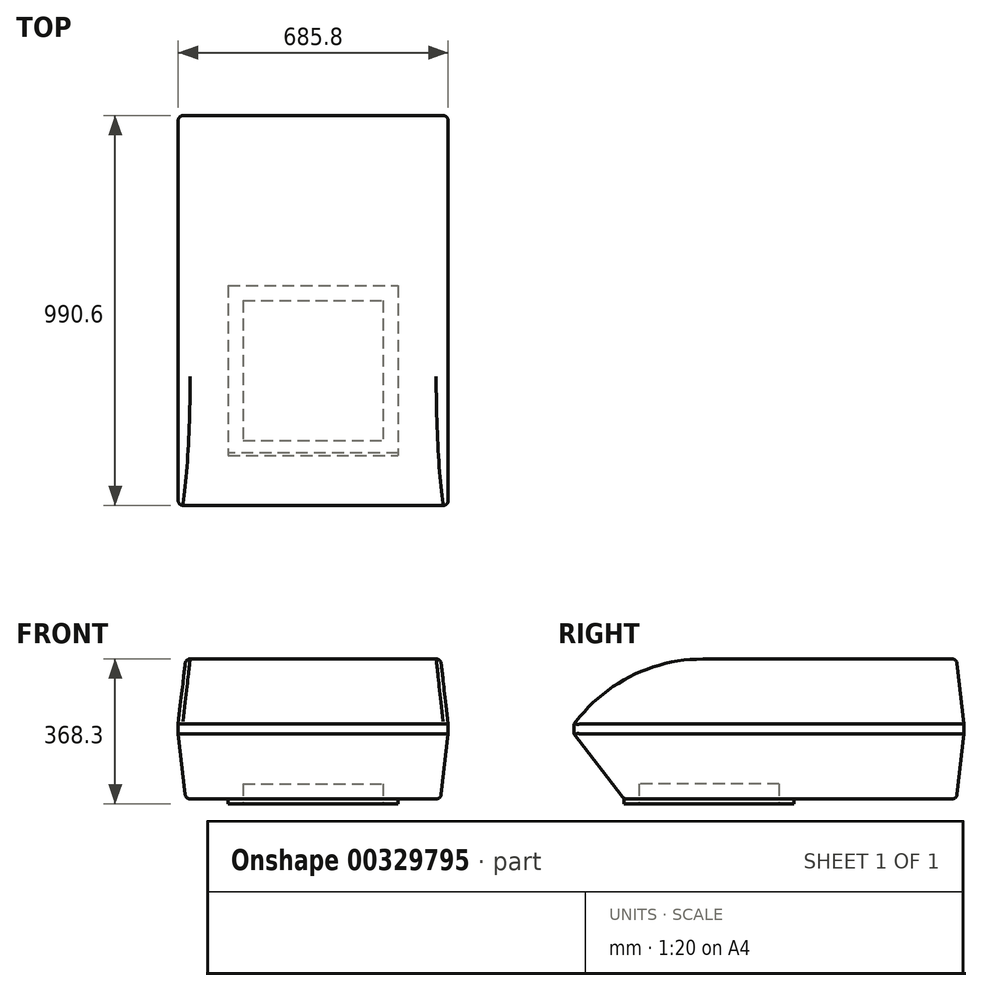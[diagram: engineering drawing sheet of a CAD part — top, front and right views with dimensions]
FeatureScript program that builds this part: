
annotation { "Feature Type Name" : "Feature", "Feature Type Description" : "" }
export const myFeature = defineFeature(function(context is Context, id is Id, definition is map)
    precondition{}
    {
        {
            var Q0;
            Q0=qCreatedBy(makeId("Top.planeOp"),FACE);
            var sketch = newSketch(context, id + "F0", { "sketchPlane" : qUnion([Q0])});
            skLineSegment(sketch, "E0.bottom", {"start": v(0, 0) * mm, "end": v(-685.8, 0) * mm});
            skLineSegment(sketch, "E0.top", {"start": v(0, 990.6) * mm, "end": v(-685.8, 990.6) * mm});
            skLineSegment(sketch, "E0.left", {"start": v(0, 0) * mm, "end": v(0, 990.6) * mm});
            skLineSegment(sketch, "E0.right", {"start": v(-685.8, 0) * mm, "end": v(-685.8, 990.6) * mm});
            skSolve(sketch);
        }
        {
            var Q0;
            Q0 = qSketchRegion(id + "F0", true);
            extrude(context, id + "F1", {"entities" : qUnion([Q0]), "depth" : 355.6 * mm});
        }
        {
            var Q0;
            Q0=makeQuery(id+"F1.opExtrude","CAP_FACE",FACE,{"disambiguationData":[OSD([sQuery(id+"F0.wireOp",EDGE,"E0.bottom"),sQuery(id+"F0.wireOp",EDGE,"E0.top"),sQuery(id+"F0.wireOp",EDGE,"E0.left"),sQuery(id+"F0.wireOp",EDGE,"E0.right")])],"isStart":true});
            var sketch = newSketch(context, id + "F2", { "sketchPlane" : qUnion([Q0])});
            skLineSegment(sketch, "E1.bottom", {"start": v(-520.7, -520.7) * mm, "end": v(-165.1, -520.7) * mm});
            skLineSegment(sketch, "E1.top", {"start": v(-520.7, -165.1) * mm, "end": v(-165.1, -165.1) * mm});
            skLineSegment(sketch, "E1.left", {"start": v(-520.7, -520.7) * mm, "end": v(-520.7, -165.1) * mm});
            skLineSegment(sketch, "E1.right", {"start": v(-165.1, -520.7) * mm, "end": v(-165.1, -165.1) * mm});
            skLineSegment(sketch, "E2.0", {"start": v(-558.8, -558.8) * mm, "end": v(-558.8, -127) * mm});
            skLineSegment(sketch, "E2.1", {"start": v(-558.8, -558.8) * mm, "end": v(-127, -558.8) * mm});
            skLineSegment(sketch, "E2.2", {"start": v(-127, -558.8) * mm, "end": v(-127, -127) * mm});
            skLineSegment(sketch, "E2.3", {"start": v(-558.8, -127) * mm, "end": v(-127, -127) * mm});
            skSolve(sketch);
        }
        {
            var Q0;
            Q0=makeQuery(id+"F1.opExtrude","CAP_EDGE",EDGE,{"disambiguationData":[OSD([sQuery(id+"F0.wireOp",EDGE,"E0.right")])],"isStart":false});
            var Q1;
            Q1=makeQuery(id+"F1.opExtrude","CAP_EDGE",EDGE,{"disambiguationData":[OSD([sQuery(id+"F0.wireOp",EDGE,"E0.left")])],"isStart":false});
            var Q2;
            Q2=makeQuery(id+"F1.opExtrude","CAP_EDGE",EDGE,{"disambiguationData":[OSD([sQuery(id+"F0.wireOp",EDGE,"E0.right")])],"isStart":true});
            var Q3;
            Q3=makeQuery(id+"F1.opExtrude","CAP_EDGE",EDGE,{"disambiguationData":[OSD([sQuery(id+"F0.wireOp",EDGE,"E0.left")])],"isStart":true});
            var Q4;
            Q4=makeQuery(id+"F1.opExtrude","CAP_EDGE",EDGE,{"disambiguationData":[OSD([sQuery(id+"F0.wireOp",EDGE,"E0.top")])],"isStart":false});
            var Q5;
            Q5=makeQuery(id+"F1.opExtrude","CAP_EDGE",EDGE,{"disambiguationData":[OSD([sQuery(id+"F0.wireOp",EDGE,"E0.top")])],"isStart":true});
            chamfer(context, id + "F3", {"entities" : qUnion([Q0, Q1, Q2, Q3, Q4, Q5]), "chamferType" : ChamferType.TWO_OFFSETS, "width1" : 165.1 * mm, "oppositeDirection" : false, "width2" : 19.05 * mm, "tangentPropagation" : true});
        }
        {
            var Q0;
            Q0=makeQuery(id+"F1.opExtrude","CAP_EDGE",EDGE,{"disambiguationData":[OSD([sQuery(id+"F0.wireOp",EDGE,"E0.bottom")])],"isStart":false});
            var Q1;
            Q1=makeQuery(id+"F1.opExtrude","CAP_EDGE",EDGE,{"disambiguationData":[OSD([sQuery(id+"F0.wireOp",EDGE,"E0.bottom")])],"isStart":true});
            chamfer(context, id + "F4", {"entities" : qUnion([Q0, Q1]), "chamferType" : ChamferType.TWO_OFFSETS, "width1" : 165.1 * mm, "oppositeDirection" : false, "width2" : 127 * mm, "tangentPropagation" : true});
        }
        {
            var Q0;
            Q0=makeQuery(id+"F1.opExtrude","CAP_FACE",FACE,{"disambiguationData":[OSD([sQuery(id+"F0.wireOp",EDGE,"E0.bottom"),sQuery(id+"F0.wireOp",EDGE,"E0.top"),sQuery(id+"F0.wireOp",EDGE,"E0.left"),sQuery(id+"F0.wireOp",EDGE,"E0.right")])],"isStart":true});
            var Q1;
            Q1=makeQuery(id+"F1.opExtrude","SWEPT_EDGE",EDGE,{"disambiguationData":[OSD([sQuery(id+"F0.wireOp",EDGE,"E0.top"),sQuery(id+"F0.wireOp",EDGE,"E0.right")])]});
            var Q2;
            Q2=makeQuery(id+"F1.opExtrude","SWEPT_EDGE",EDGE,{"disambiguationData":[OSD([sQuery(id+"F0.wireOp",EDGE,"E0.top"),sQuery(id+"F0.wireOp",EDGE,"E0.left")])]});
            var Q3;
            Q3=makeQuery(id+"F3.opChamfer","BLEND_EDGE",EDGE,{"blendedFrom":[makeQuery(id+"F1.opExtrude","CAP_EDGE",EDGE,{"disambiguationData":[OSD([sQuery(id+"F0.wireOp",EDGE,"E0.top")])],"isStart":true}),makeQuery(id+"F1.opExtrude","CAP_EDGE",EDGE,{"disambiguationData":[OSD([sQuery(id+"F0.wireOp",EDGE,"E0.right")])],"isStart":true})],"blendedInto":[]});
            var Q4;
            Q4=makeQuery(id+"F3.opChamfer","BLEND_EDGE",EDGE,{"blendedFrom":[makeQuery(id+"F1.opExtrude","CAP_EDGE",EDGE,{"disambiguationData":[OSD([sQuery(id+"F0.wireOp",EDGE,"E0.top")])],"isStart":true}),makeQuery(id+"F1.opExtrude","CAP_EDGE",EDGE,{"disambiguationData":[OSD([sQuery(id+"F0.wireOp",EDGE,"E0.left")])],"isStart":true})],"blendedInto":[]});
            var Q5;
            Q5=makeQuery(id+"F3.opChamfer","BLEND_EDGE",EDGE,{"blendedFrom":[makeQuery(id+"F1.opExtrude","CAP_EDGE",EDGE,{"disambiguationData":[OSD([sQuery(id+"F0.wireOp",EDGE,"E0.top")])],"isStart":false}),makeQuery(id+"F1.opExtrude","CAP_EDGE",EDGE,{"disambiguationData":[OSD([sQuery(id+"F0.wireOp",EDGE,"E0.left")])],"isStart":false})],"blendedInto":[]});
            var Q6;
            Q6=makeQuery(id+"F3.opChamfer","BLEND_EDGE",EDGE,{"blendedFrom":[makeQuery(id+"F1.opExtrude","CAP_EDGE",EDGE,{"disambiguationData":[OSD([sQuery(id+"F0.wireOp",EDGE,"E0.top")])],"isStart":false}),makeQuery(id+"F1.opExtrude","CAP_EDGE",EDGE,{"disambiguationData":[OSD([sQuery(id+"F0.wireOp",EDGE,"E0.right")])],"isStart":false})],"blendedInto":[]});
            var Q7;
            Q7=makeQuery(id+"F1.opExtrude","SWEPT_EDGE",EDGE,{"disambiguationData":[OSD([sQuery(id+"F0.wireOp",EDGE,"E0.bottom"),sQuery(id+"F0.wireOp",EDGE,"E0.right")])]});
            var Q8;
            {var subQ0=sQuery(id+"F0.wireOp",EDGE,"E0.right");Q8=makeQuery(id+"F4.opChamfer","BLEND_EDGE",EDGE,{"blendedFrom":[makeQuery(id+"F1.opExtrude","CAP_EDGE",EDGE,{"disambiguationData":[OSD([sQuery(id+"F0.wireOp",EDGE,"E0.bottom")])],"isStart":true}),makeQuery(id+"F3.opChamfer","BLEND_FACE",FACE,{"disambiguationData":[OSD([subQ0]),TDD([makeQuery(id+"F1.opExtrude","CAP_EDGE",EDGE,{"disambiguationData":[OSD([subQ0])],"isStart":true})])]})],"blendedInto":[makeQuery(id+"F3.opChamfer","BLEND_FACE",FACE,{"disambiguationData":[OSD([subQ0]),TDD([makeQuery(id+"F1.opExtrude","CAP_EDGE",EDGE,{"disambiguationData":[OSD([subQ0])],"isStart":true})])]})]});}
            var Q9;
            Q9=makeQuery(id+"F1.opExtrude","SWEPT_EDGE",EDGE,{"disambiguationData":[OSD([sQuery(id+"F0.wireOp",EDGE,"E0.bottom"),sQuery(id+"F0.wireOp",EDGE,"E0.left")])]});
            var Q10;
            {var subQ0=sQuery(id+"F0.wireOp",EDGE,"E0.left");Q10=makeQuery(id+"F4.opChamfer","BLEND_EDGE",EDGE,{"blendedFrom":[makeQuery(id+"F1.opExtrude","CAP_EDGE",EDGE,{"disambiguationData":[OSD([sQuery(id+"F0.wireOp",EDGE,"E0.bottom")])],"isStart":true}),makeQuery(id+"F3.opChamfer","BLEND_FACE",FACE,{"disambiguationData":[OSD([subQ0]),TDD([makeQuery(id+"F1.opExtrude","CAP_EDGE",EDGE,{"disambiguationData":[OSD([subQ0])],"isStart":true})])]})],"blendedInto":[makeQuery(id+"F3.opChamfer","BLEND_FACE",FACE,{"disambiguationData":[OSD([subQ0]),TDD([makeQuery(id+"F1.opExtrude","CAP_EDGE",EDGE,{"disambiguationData":[OSD([subQ0])],"isStart":true})])]})]});}
            var Q11;
            {var subQ0=sQuery(id+"F0.wireOp",EDGE,"E0.right");Q11=makeQuery(id+"F4.opChamfer","BLEND_EDGE",EDGE,{"blendedFrom":[makeQuery(id+"F1.opExtrude","CAP_EDGE",EDGE,{"disambiguationData":[OSD([sQuery(id+"F0.wireOp",EDGE,"E0.bottom")])],"isStart":false}),makeQuery(id+"F3.opChamfer","BLEND_FACE",FACE,{"disambiguationData":[OSD([subQ0]),TDD([makeQuery(id+"F1.opExtrude","CAP_EDGE",EDGE,{"disambiguationData":[OSD([subQ0])],"isStart":false})])]})],"blendedInto":[makeQuery(id+"F3.opChamfer","BLEND_FACE",FACE,{"disambiguationData":[OSD([subQ0]),TDD([makeQuery(id+"F1.opExtrude","CAP_EDGE",EDGE,{"disambiguationData":[OSD([subQ0])],"isStart":false})])]})]});}
            var Q12;
            {var subQ0=sQuery(id+"F0.wireOp",EDGE,"E0.left");Q12=makeQuery(id+"F4.opChamfer","BLEND_EDGE",EDGE,{"blendedFrom":[makeQuery(id+"F1.opExtrude","CAP_EDGE",EDGE,{"disambiguationData":[OSD([sQuery(id+"F0.wireOp",EDGE,"E0.bottom")])],"isStart":false}),makeQuery(id+"F3.opChamfer","BLEND_FACE",FACE,{"disambiguationData":[OSD([subQ0]),TDD([makeQuery(id+"F1.opExtrude","CAP_EDGE",EDGE,{"disambiguationData":[OSD([subQ0])],"isStart":false})])]})],"blendedInto":[makeQuery(id+"F3.opChamfer","BLEND_FACE",FACE,{"disambiguationData":[OSD([subQ0]),TDD([makeQuery(id+"F1.opExtrude","CAP_EDGE",EDGE,{"disambiguationData":[OSD([subQ0])],"isStart":false})])]})]});}
            var Q13;
            {var subQ0=sQuery(id+"F0.wireOp",EDGE,"E0.left");Q13=makeQuery(id+"F3.opChamfer","BLEND_EDGE",EDGE,{"blendedFrom":[makeQuery(id+"F1.opExtrude","CAP_EDGE",EDGE,{"disambiguationData":[OSD([subQ0])],"isStart":false}),makeQuery(id+"F1.opExtrude","CAP_FACE",FACE,{"disambiguationData":[OSD([sQuery(id+"F0.wireOp",EDGE,"E0.bottom"),sQuery(id+"F0.wireOp",EDGE,"E0.top"),subQ0,sQuery(id+"F0.wireOp",EDGE,"E0.right")])],"isStart":false})],"blendedInto":[makeQuery(id+"F1.opExtrude","CAP_FACE",FACE,{"disambiguationData":[OSD([sQuery(id+"F0.wireOp",EDGE,"E0.bottom"),sQuery(id+"F0.wireOp",EDGE,"E0.top"),subQ0,sQuery(id+"F0.wireOp",EDGE,"E0.right")])],"isStart":false})]});}
            var Q14;
            {var subQ0=sQuery(id+"F0.wireOp",EDGE,"E0.top");Q14=makeQuery(id+"F3.opChamfer","BLEND_EDGE",EDGE,{"blendedFrom":[makeQuery(id+"F1.opExtrude","CAP_EDGE",EDGE,{"disambiguationData":[OSD([subQ0])],"isStart":false}),makeQuery(id+"F1.opExtrude","CAP_FACE",FACE,{"disambiguationData":[OSD([sQuery(id+"F0.wireOp",EDGE,"E0.bottom"),subQ0,sQuery(id+"F0.wireOp",EDGE,"E0.left"),sQuery(id+"F0.wireOp",EDGE,"E0.right")])],"isStart":false})],"blendedInto":[makeQuery(id+"F1.opExtrude","CAP_FACE",FACE,{"disambiguationData":[OSD([sQuery(id+"F0.wireOp",EDGE,"E0.bottom"),subQ0,sQuery(id+"F0.wireOp",EDGE,"E0.left"),sQuery(id+"F0.wireOp",EDGE,"E0.right")])],"isStart":false})]});}
            var Q15;
            {var subQ0=sQuery(id+"F0.wireOp",EDGE,"E0.right");Q15=makeQuery(id+"F3.opChamfer","BLEND_EDGE",EDGE,{"blendedFrom":[makeQuery(id+"F1.opExtrude","CAP_EDGE",EDGE,{"disambiguationData":[OSD([subQ0])],"isStart":false}),makeQuery(id+"F1.opExtrude","CAP_FACE",FACE,{"disambiguationData":[OSD([sQuery(id+"F0.wireOp",EDGE,"E0.bottom"),sQuery(id+"F0.wireOp",EDGE,"E0.top"),sQuery(id+"F0.wireOp",EDGE,"E0.left"),subQ0])],"isStart":false})],"blendedInto":[makeQuery(id+"F1.opExtrude","CAP_FACE",FACE,{"disambiguationData":[OSD([sQuery(id+"F0.wireOp",EDGE,"E0.bottom"),sQuery(id+"F0.wireOp",EDGE,"E0.top"),sQuery(id+"F0.wireOp",EDGE,"E0.left"),subQ0])],"isStart":false})]});}
            fillet(context, id + "F5", {"entities" : qUnion([Q0, Q1, Q2, Q3, Q4, Q5, Q6, Q7, Q8, Q9, Q10, Q11, Q12, Q13, Q14, Q15]), "radius" : 12.7 * mm, "tangentPropagation" : true, "allowEdgeOverflow" : false});
        }
        {
            var Q0;
            {var subQ0=sQuery(id+"F0.wireOp",EDGE,"E0.bottom");Q0=makeQuery(id+"F4.opChamfer","BLEND_EDGE",EDGE,{"blendedFrom":[makeQuery(id+"F1.opExtrude","CAP_EDGE",EDGE,{"disambiguationData":[OSD([subQ0])],"isStart":false}),makeQuery(id+"F1.opExtrude","CAP_FACE",FACE,{"disambiguationData":[OSD([subQ0,sQuery(id+"F0.wireOp",EDGE,"E0.top"),sQuery(id+"F0.wireOp",EDGE,"E0.left"),sQuery(id+"F0.wireOp",EDGE,"E0.right")])],"isStart":false})],"blendedInto":[makeQuery(id+"F1.opExtrude","CAP_FACE",FACE,{"disambiguationData":[OSD([subQ0,sQuery(id+"F0.wireOp",EDGE,"E0.top"),sQuery(id+"F0.wireOp",EDGE,"E0.left"),sQuery(id+"F0.wireOp",EDGE,"E0.right")])],"isStart":false})]});}
            fillet(context, id + "F6", {"entities" : qUnion([Q0]), "radius" : 406.4 * mm, "tangentPropagation" : true, "allowEdgeOverflow" : false});
        }
        {
            var Q0;
            Q0=makeQuery(id+"F2.imprint","IMPRINT",FACE,{"disambiguationData":[TD([[makeQuery(id+"F2.imprint","IMPRINT",EDGE,{"derivedFrom":sQuery(id+"F2.wireOp",EDGE,"E1.bottom")}),1.0]])]});
            extrude(context, id + "F7", {"entities" : qUnion([Q0]), "operationType" : NewBodyOperationType.REMOVE, "oppositeDirection" : true, "depth" : 38.1 * mm});
        }
        {
            var Q0;
            Q0=makeQuery(id+"F2.imprint","IMPRINT",FACE,{"disambiguationData":[TD([[makeQuery(id+"F2.imprint","IMPRINT",EDGE,{"derivedFrom":sQuery(id+"F2.wireOp",EDGE,"E1.bottom")}),-1.0]])]});
            extrude(context, id + "F8", {"entities" : qUnion([Q0]), "operationType" : NewBodyOperationType.ADD, "depth" : 12.7 * mm});
        }
    });
